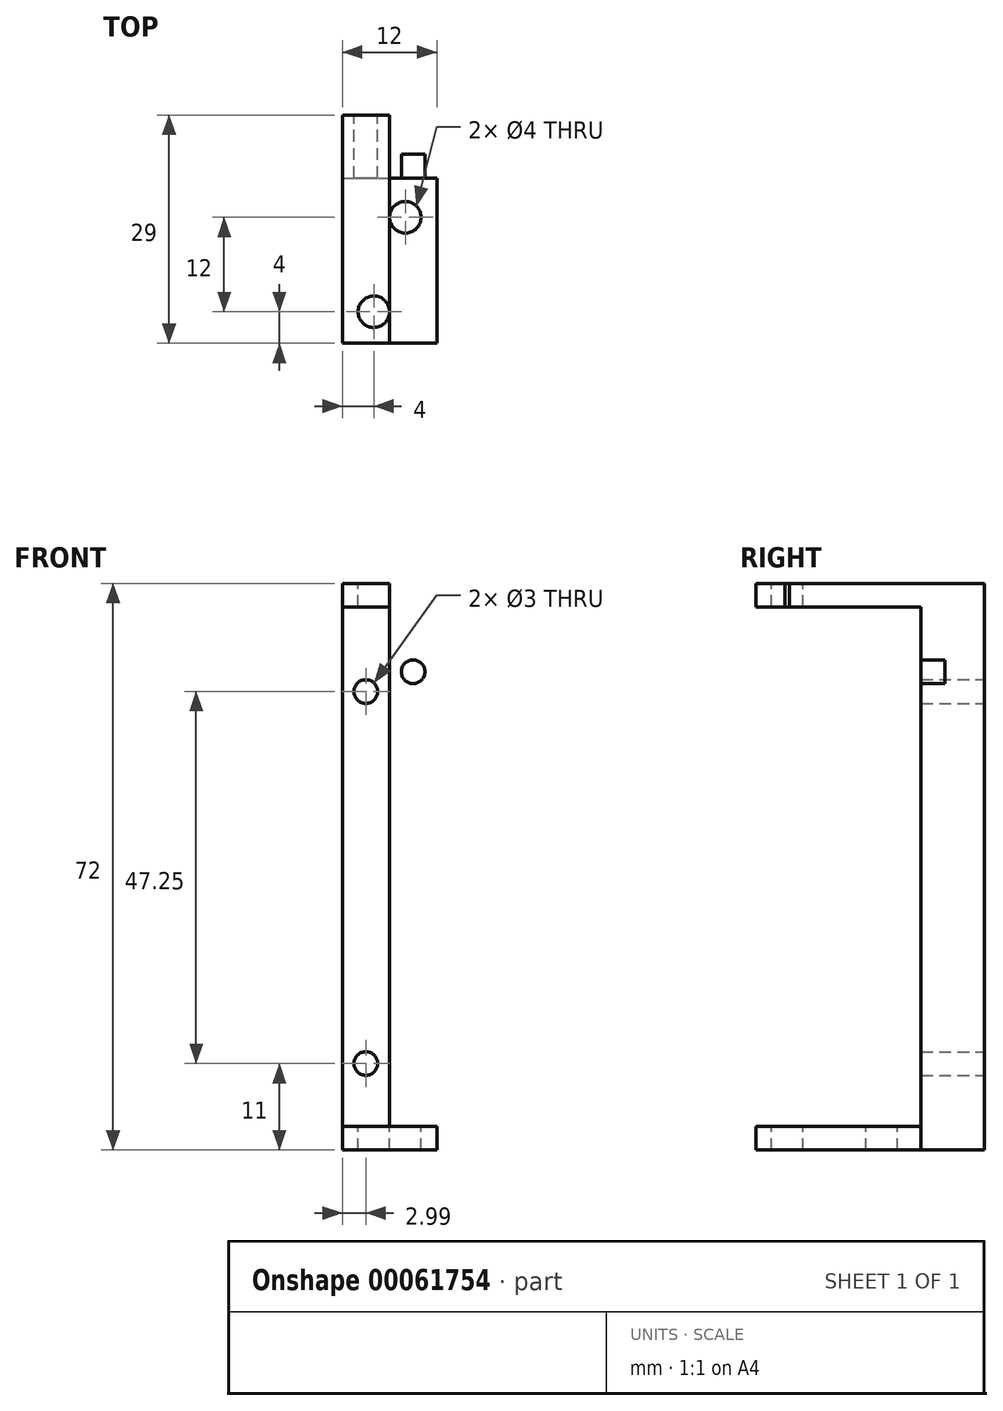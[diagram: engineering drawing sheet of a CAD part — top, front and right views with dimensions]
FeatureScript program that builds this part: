
annotation { "Feature Type Name" : "Feature", "Feature Type Description" : "" }
export const myFeature = defineFeature(function(context is Context, id is Id, definition is map)
    precondition{}
    {
        {
            var Q0;
            Q0=qCreatedBy(makeId("Right.planeOp"),FACE);
            var sketch = newSketch(context, id + "F0", { "sketchPlane" : qUnion([Q0])});
            skLineSegment(sketch, "E0", {"start": v(-10.5, 37.5) * mm, "end": v(18.5, 37.5) * mm});
            skLineSegment(sketch, "E1", {"start": v(18.5, 37.5) * mm, "end": v(18.5, -34.5) * mm});
            skLineSegment(sketch, "E2.0", {"start": v(10.5, 34.5) * mm, "end": v(10.5, -34.5) * mm});
            skLineSegment(sketch, "E2.1", {"start": v(-10.5, 34.5) * mm, "end": v(10.5, 34.5) * mm});
            skLineSegment(sketch, "E3", {"start": v(-10.5, 37.5) * mm, "end": v(-10.5, 34.5) * mm});
            skLineSegment(sketch, "E4", {"start": v(18.5, -34.5) * mm, "end": v(10.5, -34.5) * mm});
            skLineSegment(sketch, "E5", {"start": v(10.5, 0) * mm, "end": v(-14.36, 0) * mm, "construction": true});
            skLineSegment(sketch, "E6", {"start": v(0, 34.5) * mm, "end": v(0, -1.72) * mm, "construction": true});
            skSolve(sketch);
        }
        {
            var Q0;
            Q0=makeQuery(id+"F0.imprint","IMPRINT",FACE,{"disambiguationData":[TD([[makeQuery(id+"F0.imprint","IMPRINT",EDGE,{"derivedFrom":sQuery(id+"F0.wireOp",EDGE,"E0")}),-1.0]])]});
            extrude(context, id + "F1", {"entities" : qUnion([Q0]), "depth" : 12 * mm});
        }
        {
            var Q0;
            Q0=makeQuery(id+"F1.opExtrude","SWEPT_FACE",FACE,{"disambiguationData":[OSD([sQuery(id+"F0.wireOp",EDGE,"E0")])]});
            var sketch = newSketch(context, id + "F2", { "sketchPlane" : qUnion([Q0])});
            skLineSegment(sketch, "E7.bottom", {"start": v(0, 18.5) * mm, "end": v(6.02, 18.5) * mm});
            skLineSegment(sketch, "E7.top", {"start": v(0, 13.5) * mm, "end": v(6.02, 13.5) * mm});
            skLineSegment(sketch, "E7.left", {"start": v(0, 18.5) * mm, "end": v(0, 13.5) * mm});
            skLineSegment(sketch, "E7.right", {"start": v(6.02, 18.5) * mm, "end": v(6.02, 13.5) * mm});
            skSolve(sketch);
        }
        {
            var Q0;
            Q0=makeQuery(id+"F2.imprint","IMPRINT",FACE,{"disambiguationData":[TD([[makeQuery(id+"F2.imprint","IMPRINT",EDGE,{"derivedFrom":sQuery(id+"F2.wireOp",EDGE,"E7.bottom")}),1.0]])]});
            extrude(context, id + "F3", {"entities" : qUnion([Q0]), "operationType" : NewBodyOperationType.REMOVE, "oppositeDirection" : true, "depth" : 72 * mm});
        }
        {
            var Q0;
            Q0=makeQuery(id+"F1.opExtrude","SWEPT_FACE",FACE,{"disambiguationData":[OSD([sQuery(id+"F0.wireOp",EDGE,"E1")])]});
            var sketch = newSketch(context, id + "F4", { "sketchPlane" : qUnion([Q0])});
            skCircle(sketch, "E8", {"center": v(-9, 23.75) * mm, "radius": 1.5 * mm});
            skCircle(sketch, "E9", {"center": v(-9, -23.5) * mm, "radius": 1.5 * mm});
            skLineSegment(sketch, "E10", {"start": v(-9, 23.75) * mm, "end": v(-9, -23.5) * mm, "construction": true});
            skPoint(sketch, "E11", {"position": v(-9, 37.5) * mm});
            skLineSegment(sketch, "E12", {"start": v(-9, 23.75) * mm, "end": v(-9, 37.5) * mm, "construction": true});
            skSolve(sketch);
        }
        {
            var Q0;
            Q0=makeQuery(id+"F4.imprint","IMPRINT",FACE,{"disambiguationData":[TD([[makeQuery(id+"F4.imprint","IMPRINT",EDGE,{"derivedFrom":sQuery(id+"F4.wireOp",EDGE,"E8")}),1.0]])]});
            var Q1;
            Q1=makeQuery(id+"F4.imprint","IMPRINT",FACE,{"disambiguationData":[TD([[makeQuery(id+"F4.imprint","IMPRINT",EDGE,{"derivedFrom":sQuery(id+"F4.wireOp",EDGE,"E9")}),1.0]])]});
            extrude(context, id + "F5", {"entities" : qUnion([Q0, Q1]), "operationType" : NewBodyOperationType.REMOVE, "oppositeDirection" : true, "depth" : 25 * mm});
        }
        {
            var Q0;
            Q0=makeQuery(id+"F3.boolean.opBoolean","COPY",FACE,{"derivedFrom":makeQuery(id+"F3.opExtrude","SWEPT_FACE",FACE,{"disambiguationData":[OSD([sQuery(id+"F2.wireOp",EDGE,"E7.top")])]})});
            var sketch = newSketch(context, id + "F6", { "sketchPlane" : qUnion([Q0])});
            skCircle(sketch, "E13.0", {"center": v(-3, 26.27) * mm, "radius": 1.5 * mm});
            skCircle(sketch, "E14.0", {"center": v(-3, -23.27) * mm, "radius": 1.5 * mm});
            skLineSegment(sketch, "E15", {"start": v(-3, 37.5) * mm, "end": v(-3, 26.27) * mm, "construction": true});
            skLineSegment(sketch, "E16", {"start": v(-3, 26.27) * mm, "end": v(-3, -23.27) * mm, "construction": true});
            skSolve(sketch);
        }
        {
            var Q0;
            Q0=makeQuery(id+"F6.imprint","IMPRINT",FACE,{"disambiguationData":[TD([[makeQuery(id+"F6.imprint","IMPRINT",EDGE,{"derivedFrom":sQuery(id+"F6.wireOp",EDGE,"E14.0")}),1.0]])]});
            var Q1;
            Q1=makeQuery(id+"F6.imprint","IMPRINT",FACE,{"disambiguationData":[TD([[makeQuery(id+"F6.imprint","IMPRINT",EDGE,{"derivedFrom":sQuery(id+"F6.wireOp",EDGE,"E13.0")}),-1.0]])]});
            extrude(context, id + "F7", {"entities" : qUnion([Q0, Q1]), "operationType" : NewBodyOperationType.REMOVE, "oppositeDirection" : true, "depth" : 25 * mm});
        }
        {
            var Q0;
            Q0=makeQuery(id+"F1.opExtrude","SWEPT_FACE",FACE,{"disambiguationData":[OSD([sQuery(id+"F0.wireOp",EDGE,"E2.0")])]});
            var sketch = newSketch(context, id + "F8", { "sketchPlane" : qUnion([Q0])});
            skLineSegment(sketch, "E17.bottom", {"start": v(12, -34.5) * mm, "end": v(0, -34.5) * mm});
            skLineSegment(sketch, "E17.top", {"start": v(12, -31.5) * mm, "end": v(0, -31.5) * mm});
            skLineSegment(sketch, "E17.left", {"start": v(12, -34.5) * mm, "end": v(12, -31.5) * mm});
            skLineSegment(sketch, "E17.right", {"start": v(0, -34.5) * mm, "end": v(0, -31.5) * mm});
            skSolve(sketch);
        }
        {
            var Q0;
            Q0=makeQuery(id+"F8.imprint","IMPRINT",FACE,{"disambiguationData":[TD([[makeQuery(id+"F8.imprint","IMPRINT",EDGE,{"derivedFrom":sQuery(id+"F8.wireOp",EDGE,"E17.bottom")}),-1.0]])]});
            extrude(context, id + "F9", {"entities" : qUnion([Q0]), "operationType" : NewBodyOperationType.ADD, "depth" : 21 * mm});
        }
        {
            var Q0;
            Q0=makeQuery(id+"F1.opExtrude","SWEPT_FACE",FACE,{"disambiguationData":[OSD([sQuery(id+"F0.wireOp",EDGE,"E0")])]});
            var sketch = newSketch(context, id + "F10", { "sketchPlane" : qUnion([Q0])});
            skCircle(sketch, "E18", {"center": v(4, 5.5) * mm, "radius": 2 * mm});
            skCircle(sketch, "E19", {"center": v(8, -6.5) * mm, "radius": 2 * mm});
            skSolve(sketch);
        }
        {
            var Q0;
            Q0=makeQuery(id+"F10.imprint","IMPRINT",FACE,{"disambiguationData":[TD([[makeQuery(id+"F10.imprint","IMPRINT",EDGE,{"derivedFrom":sQuery(id+"F10.wireOp",EDGE,"E18")}),1.0]])]});
            var Q1;
            Q1=makeQuery(id+"F10.imprint","IMPRINT",FACE,{"disambiguationData":[TD([[makeQuery(id+"F10.imprint","IMPRINT",EDGE,{"derivedFrom":sQuery(id+"F10.wireOp",EDGE,"E19")}),1.0]])]});
            extrude(context, id + "F11", {"entities" : qUnion([Q0, Q1]), "operationType" : NewBodyOperationType.REMOVE, "oppositeDirection" : true, "depth" : 72 * mm});
        }
        {
            var Q0;
            Q0=makeQuery(id+"F1.opExtrude","SWEPT_BODY",BODY,{"disambiguationData":[OSD([sQuery(id+"F0.wireOp",EDGE,"E0"),sQuery(id+"F0.wireOp",EDGE,"E1"),sQuery(id+"F0.wireOp",EDGE,"E2.0"),sQuery(id+"F0.wireOp",EDGE,"E2.1"),sQuery(id+"F0.wireOp",EDGE,"E3"),sQuery(id+"F0.wireOp",EDGE,"E4")])]});
            var Q1;
            Q1=makeQuery(id+"F1.opExtrude","CAP_FACE",FACE,{"disambiguationData":[OSD([sQuery(id+"F0.wireOp",EDGE,"E0"),sQuery(id+"F0.wireOp",EDGE,"E1"),sQuery(id+"F0.wireOp",EDGE,"E2.0"),sQuery(id+"F0.wireOp",EDGE,"E2.1"),sQuery(id+"F0.wireOp",EDGE,"E3"),sQuery(id+"F0.wireOp",EDGE,"E4")])],"isStart":false});
            mirror(context, id + "F12", {"entities" : qUnion([Q0]), "mirrorPlane" : qUnion([Q1])});
        }
        {
            var Q0;
            Q0=makeQuery(id+"F1.opExtrude","SWEPT_BODY",BODY,{"disambiguationData":[OSD([sQuery(id+"F0.wireOp",EDGE,"E0"),sQuery(id+"F0.wireOp",EDGE,"E1"),sQuery(id+"F0.wireOp",EDGE,"E2.0"),sQuery(id+"F0.wireOp",EDGE,"E2.1"),sQuery(id+"F0.wireOp",EDGE,"E3"),sQuery(id+"F0.wireOp",EDGE,"E4")])]});
            deleteBodies(context, id + "F13", {"entities" : qUnion([Q0])});
        }
    });
